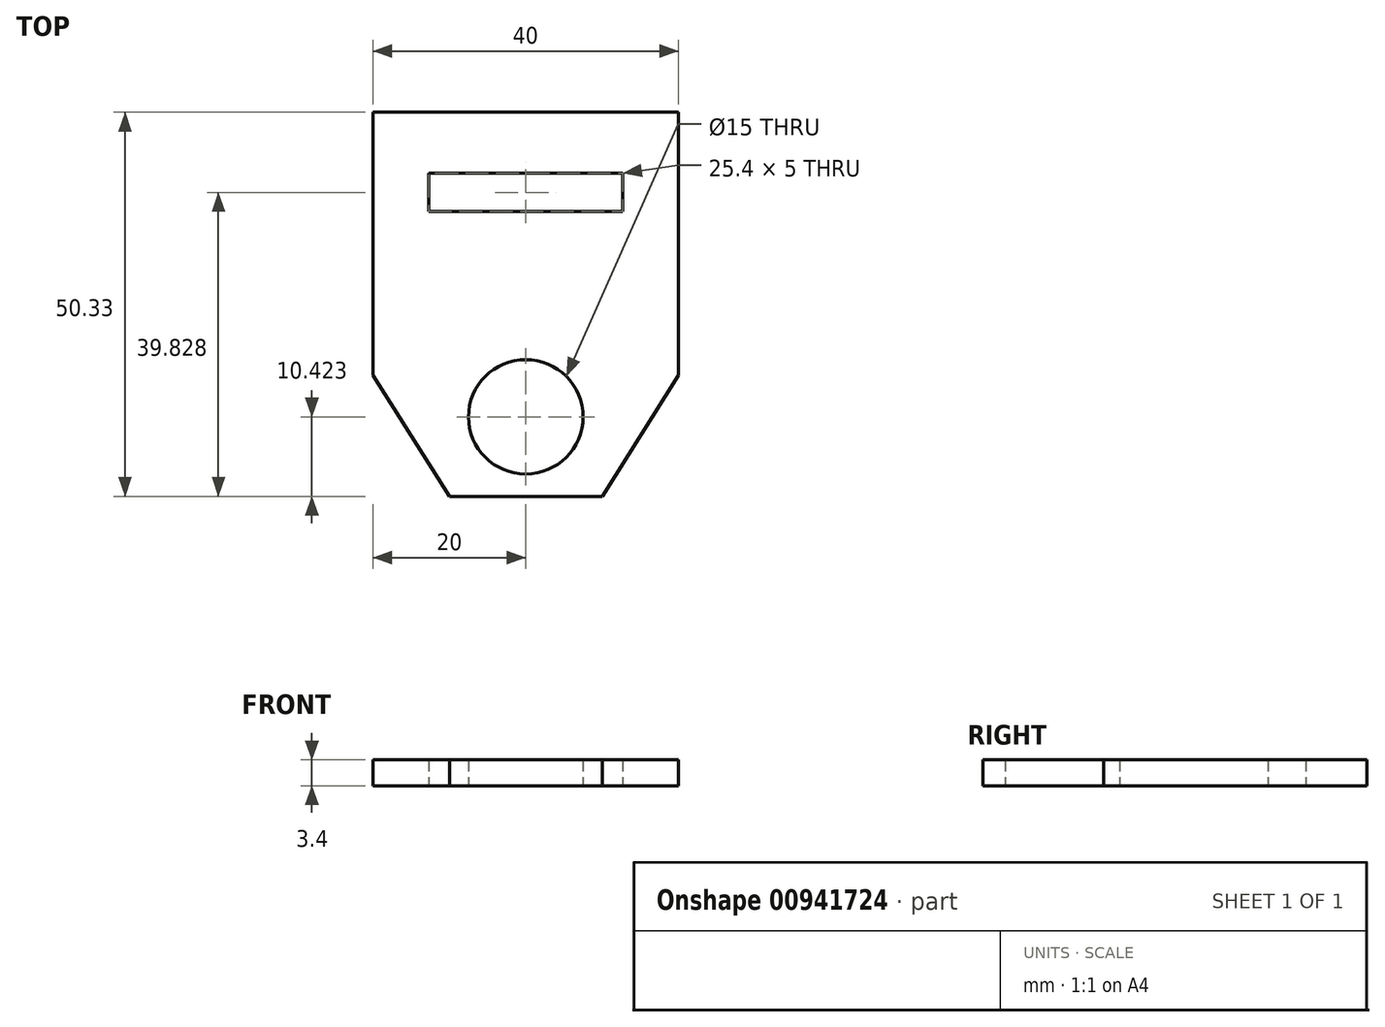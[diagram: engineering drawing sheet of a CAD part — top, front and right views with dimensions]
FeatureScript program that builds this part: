
annotation { "Feature Type Name" : "Feature", "Feature Type Description" : "" }
export const myFeature = defineFeature(function(context is Context, id is Id, definition is map)
    precondition{}
    {
        {
            var Q0;
            Q0=qCreatedBy(makeId("Top.planeOp"),FACE);
            var sketch = newSketch(context, id + "F0", { "sketchPlane" : qUnion([Q0])});
            skLineSegment(sketch, "E0.bottom", {"start": v(20, -17.25) * mm, "end": v(-20, -17.25) * mm});
            skLineSegment(sketch, "E0.top", {"start": v(20, 17.25) * mm, "end": v(-20, 17.25) * mm});
            skLineSegment(sketch, "E0.left", {"start": v(20, -17.25) * mm, "end": v(20, 17.25) * mm});
            skLineSegment(sketch, "E0.right", {"start": v(-20, -17.25) * mm, "end": v(-20, 17.25) * mm});
            skPoint(sketch, "E0.middle", {"position": v(0, 0) * mm});
            skLineSegment(sketch, "E1.bottom", {"start": v(-20, 17.25) * mm, "end": v(20, 17.25) * mm});
            skLineSegment(sketch, "E1.top", {"start": v(-20, 17.25) * mm, "end": v(20, 17.25) * mm});
            skLineSegment(sketch, "E1.left", {"start": v(-20, 17.25) * mm, "end": v(-20, 17.25) * mm});
            skLineSegment(sketch, "E1.right", {"start": v(20, 17.25) * mm, "end": v(20, 17.25) * mm});
            skPoint(sketch, "E1.middle", {"position": v(0, 17.25) * mm});
            skLineSegment(sketch, "E2.bottom", {"start": v(12.7, 4.25) * mm, "end": v(12.7, 4.25) * mm});
            skLineSegment(sketch, "E2.top", {"start": v(12.7, 9.25) * mm, "end": v(0, 9.25) * mm});
            skLineSegment(sketch, "E2.left", {"start": v(12.7, 4.25) * mm, "end": v(12.7, 9.25) * mm});
            skLineSegment(sketch, "E2.right", {"start": v(-12.7, 4.25) * mm, "end": v(-12.7, 4.25) * mm});
            skPoint(sketch, "E2.middle", {"position": v(0, 6.75) * mm});
            skLineSegment(sketch, "E3", {"start": v(0, -33.08) * mm, "end": v(10, -33.08) * mm});
            skLineSegment(sketch, "E4", {"start": v(10, -33.08) * mm, "end": v(-10, -33.08) * mm});
            skLineSegment(sketch, "E5", {"start": v(20, -17.25) * mm, "end": v(10, -33.08) * mm});
            skLineSegment(sketch, "E6", {"start": v(-20, -17.25) * mm, "end": v(-10, -33.08) * mm});
            skCircle(sketch, "E7", {"center": v(0, -22.66) * mm, "radius": 7.5 * mm});
            skLineSegment(sketch, "E8", {"start": v(0, 9.25) * mm, "end": v(-12.7, 9.25) * mm});
            skLineSegment(sketch, "E9", {"start": v(-12.7, 4.25) * mm, "end": v(-12.7, 9.25) * mm});
            skLineSegment(sketch, "E10", {"start": v(12.7, 4.25) * mm, "end": v(-12.7, 4.25) * mm});
            skSolve(sketch);
        }
        {
            var Q0;
            {var subQ4=sQuery(id+"F0.wireOp",EDGE,"E0.left");Q0=makeQuery(id+"F0.imprint","IMPRINT",FACE,{"disambiguationData":[TD([[makeQuery(id+"F0.imprint","IMPRINT",EDGE,{"derivedFrom":subQ4}),1.0]])]});}
            var Q1;
            {var subQ0=sQuery(id+"F0.wireOp",EDGE,"E5");Q1=makeQuery(id+"F0.imprint","IMPRINT",FACE,{"disambiguationData":[TD([[makeQuery(id+"F0.imprint","IMPRINT",EDGE,{"derivedFrom":subQ0}),-1.0]])]});}
            extrude(context, id + "F1", {"entities" : qUnion([Q0, Q1]), "depth" : 3.4 * mm, "offsetDistance" : 25 * mm});
        }
        {
            var Q0;
            Q0 = qSketchRegion(id + "F0", true);
            extrude(context, id + "F2", {"entities" : qUnion([Q0]), "operationType" : NewBodyOperationType.ADD, "depth" : 3.4 * mm, "offsetDistance" : 25 * mm});
        }
    });
